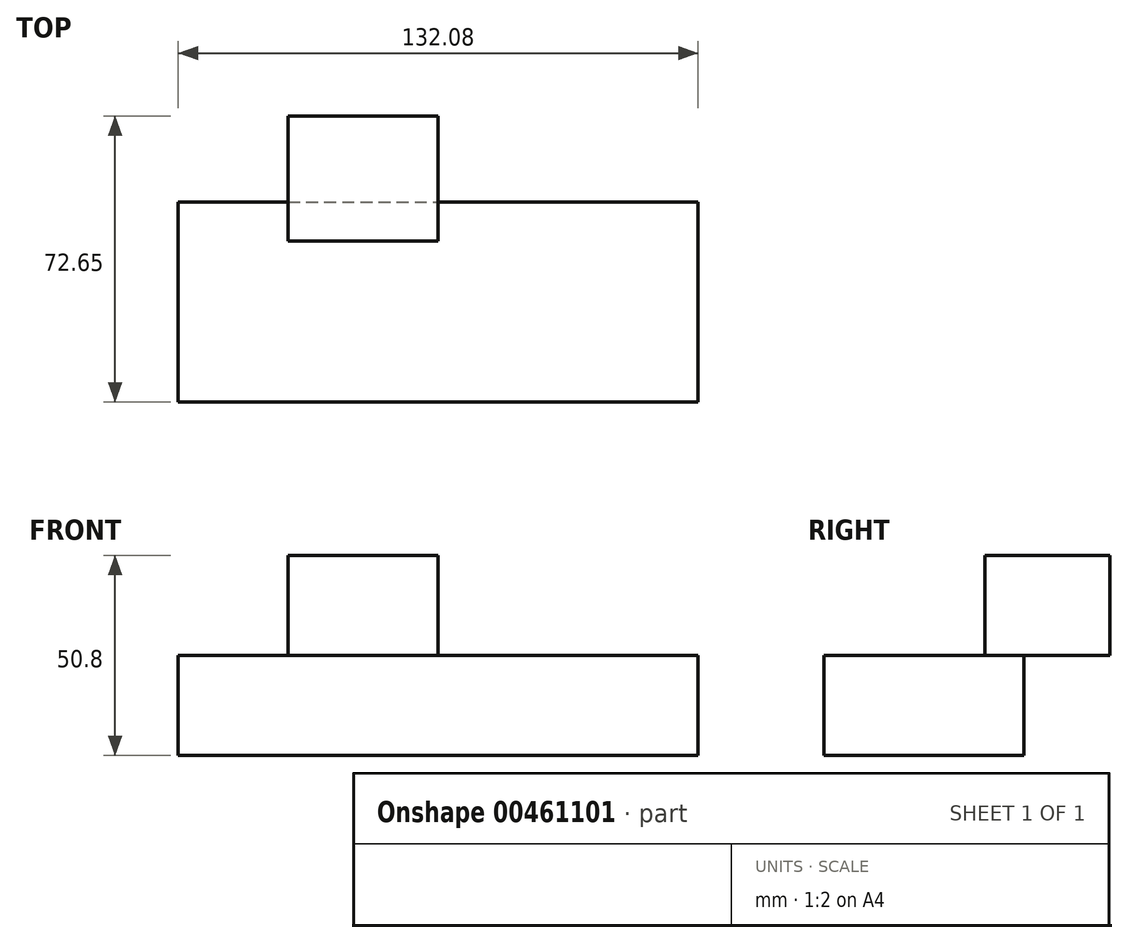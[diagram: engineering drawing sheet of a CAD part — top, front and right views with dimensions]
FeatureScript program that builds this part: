
annotation { "Feature Type Name" : "Feature", "Feature Type Description" : "" }
export const myFeature = defineFeature(function(context is Context, id is Id, definition is map)
    precondition{}
    {
        {
            var Q0;
            Q0=qCreatedBy(makeId("Top.planeOp"),FACE);
            var sketch = newSketch(context, id + "F0", { "sketchPlane" : qUnion([Q0])});
            skLineSegment(sketch, "E0.bottom", {"start": v(-148.1, 61.95) * mm, "end": v(-16.03, 61.95) * mm});
            skLineSegment(sketch, "E0.top", {"start": v(-148.1, 11.15) * mm, "end": v(-16.03, 11.15) * mm});
            skLineSegment(sketch, "E0.left", {"start": v(-148.1, 61.95) * mm, "end": v(-148.1, 11.15) * mm});
            skLineSegment(sketch, "E0.right", {"start": v(-16.03, 61.95) * mm, "end": v(-16.03, 11.15) * mm});
            skSolve(sketch);
        }
        {
            var Q0;
            Q0 = qSketchRegion(id + "F0", true);
            extrude(context, id + "F1", {"entities" : qUnion([Q0]), "depth" : 25.4 * mm});
        }
        {
            var Q0;
            Q0=makeQuery(id+"F1.opExtrude","CAP_FACE",FACE,{"disambiguationData":[OSD([sQuery(id+"F0.wireOp",EDGE,"E0.bottom"),sQuery(id+"F0.wireOp",EDGE,"E0.top"),sQuery(id+"F0.wireOp",EDGE,"E0.left"),sQuery(id+"F0.wireOp",EDGE,"E0.right")])],"isStart":false});
            var sketch = newSketch(context, id + "F2", { "sketchPlane" : qUnion([Q0])});
            skLineSegment(sketch, "E1.bottom", {"start": v(-120.2, 83.8) * mm, "end": v(-82.1, 83.8) * mm});
            skLineSegment(sketch, "E1.top", {"start": v(-120.2, 52.05) * mm, "end": v(-82.1, 52.05) * mm});
            skLineSegment(sketch, "E1.left", {"start": v(-120.2, 83.8) * mm, "end": v(-120.2, 52.05) * mm});
            skLineSegment(sketch, "E1.right", {"start": v(-82.1, 83.8) * mm, "end": v(-82.1, 52.05) * mm});
            skSolve(sketch);
        }
        {
            var Q0;
            Q0 = qSketchRegion(id + "F2", true);
            extrude(context, id + "F3", {"entities" : qUnion([Q0]), "operationType" : NewBodyOperationType.ADD, "depth" : 25.4 * mm});
        }
        {
            var Q0;
            Q0 = qSketchRegion(id + "F2", true);
            extrude(context, id + "F4", {"entities" : qUnion([Q0]), "operationType" : NewBodyOperationType.ADD, "depth" : 25.4 * mm});
        }
    });
